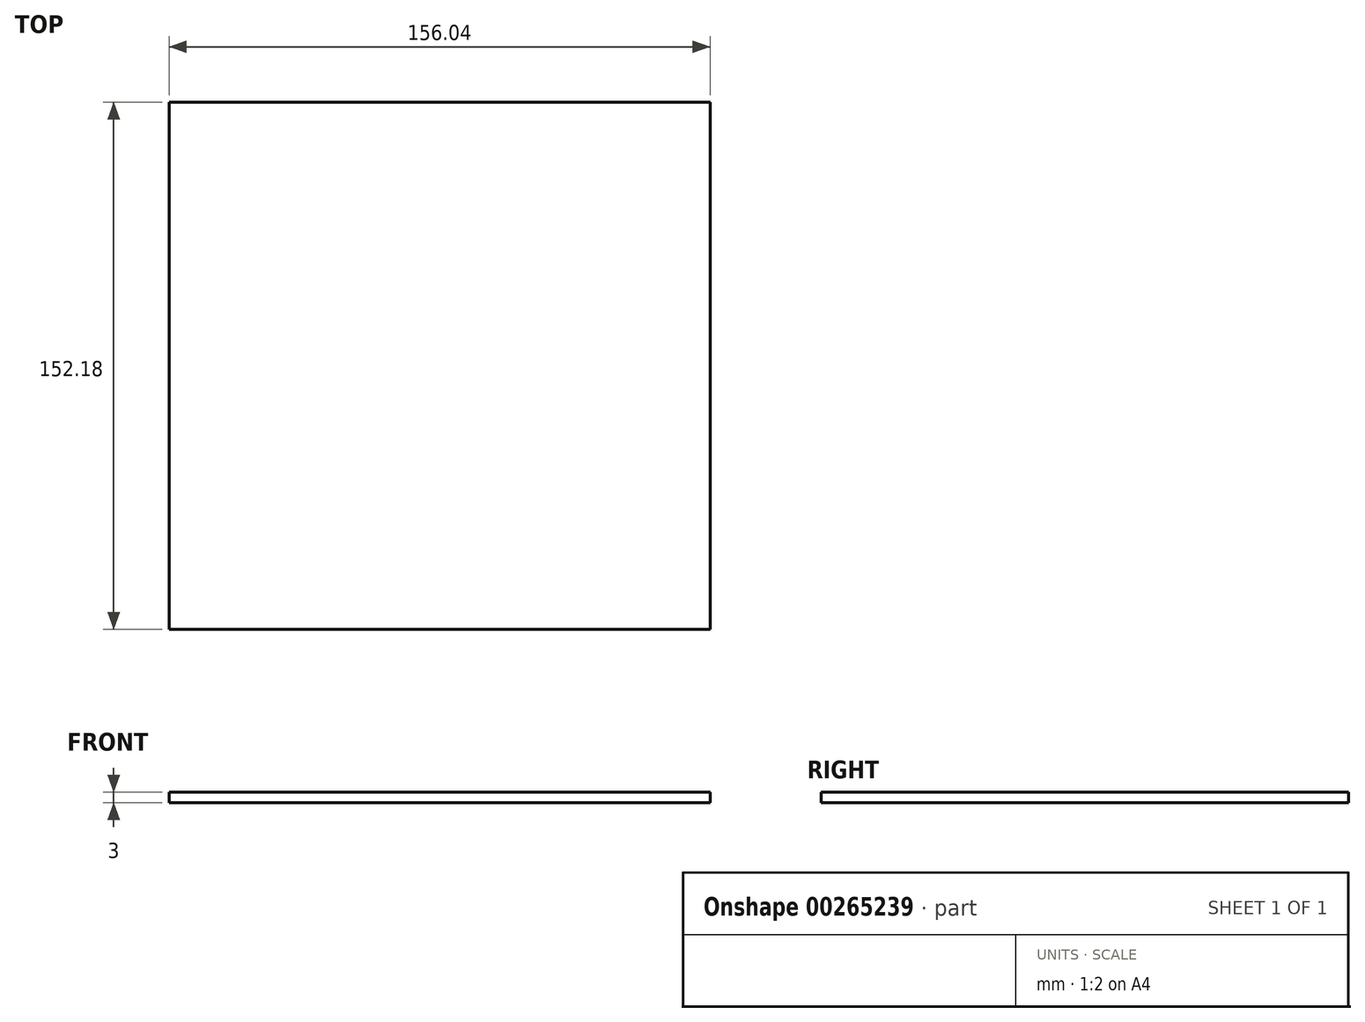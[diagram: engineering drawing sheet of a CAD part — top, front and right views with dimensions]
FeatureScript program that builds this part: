
annotation { "Feature Type Name" : "Feature", "Feature Type Description" : "" }
export const myFeature = defineFeature(function(context is Context, id is Id, definition is map)
    precondition{}
    {
        {
            var Q0;
            Q0=qCreatedBy(makeId("Top.planeOp"),FACE);
            var sketch = newSketch(context, id + "F0", { "sketchPlane" : qUnion([Q0])});
            skLineSegment(sketch, "E0.bottom", {"start": v(78.02, -76.09) * mm, "end": v(-78.02, -76.09) * mm});
            skLineSegment(sketch, "E0.top", {"start": v(78.02, 76.09) * mm, "end": v(-78.02, 76.09) * mm});
            skLineSegment(sketch, "E0.left", {"start": v(78.02, -76.09) * mm, "end": v(78.02, 76.09) * mm});
            skLineSegment(sketch, "E0.right", {"start": v(-78.02, -76.09) * mm, "end": v(-78.02, 76.09) * mm});
            skPoint(sketch, "E0.middle", {"position": v(0, 0) * mm});
            skSolve(sketch);
        }
        {
            var Q0;
            Q0 = qSketchRegion(id + "F0", true);
            extrude(context, id + "F1", {"entities" : qUnion([Q0]), "depth" : 3 * mm});
        }
    });
